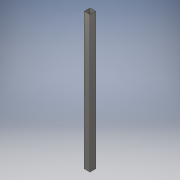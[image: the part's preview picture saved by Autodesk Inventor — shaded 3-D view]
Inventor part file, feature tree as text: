
AUTODESK INVENTOR PART (.ipt)
format: ipt  version: 2019 (Build 230136000, 136)  size: 101,376 bytes
history: native  units: mm
features: extrude x1, sketch x1
ambient origin geometry x8: Origin, YZ Plane, XZ Plane, XY Plane, X Axis, Y Axis, Z Axis, Center Point
bodies: Solid1 (feature_tree)
feature tree (2):
  extrude  "Extrusion1"  Depth=30.0mm
  sketch  "Sketch1"  dims[d0=30.0mm d1=30.0mm d2=2.5mm d3=2.5mm d4=690.0mm d5=0.0mm]
